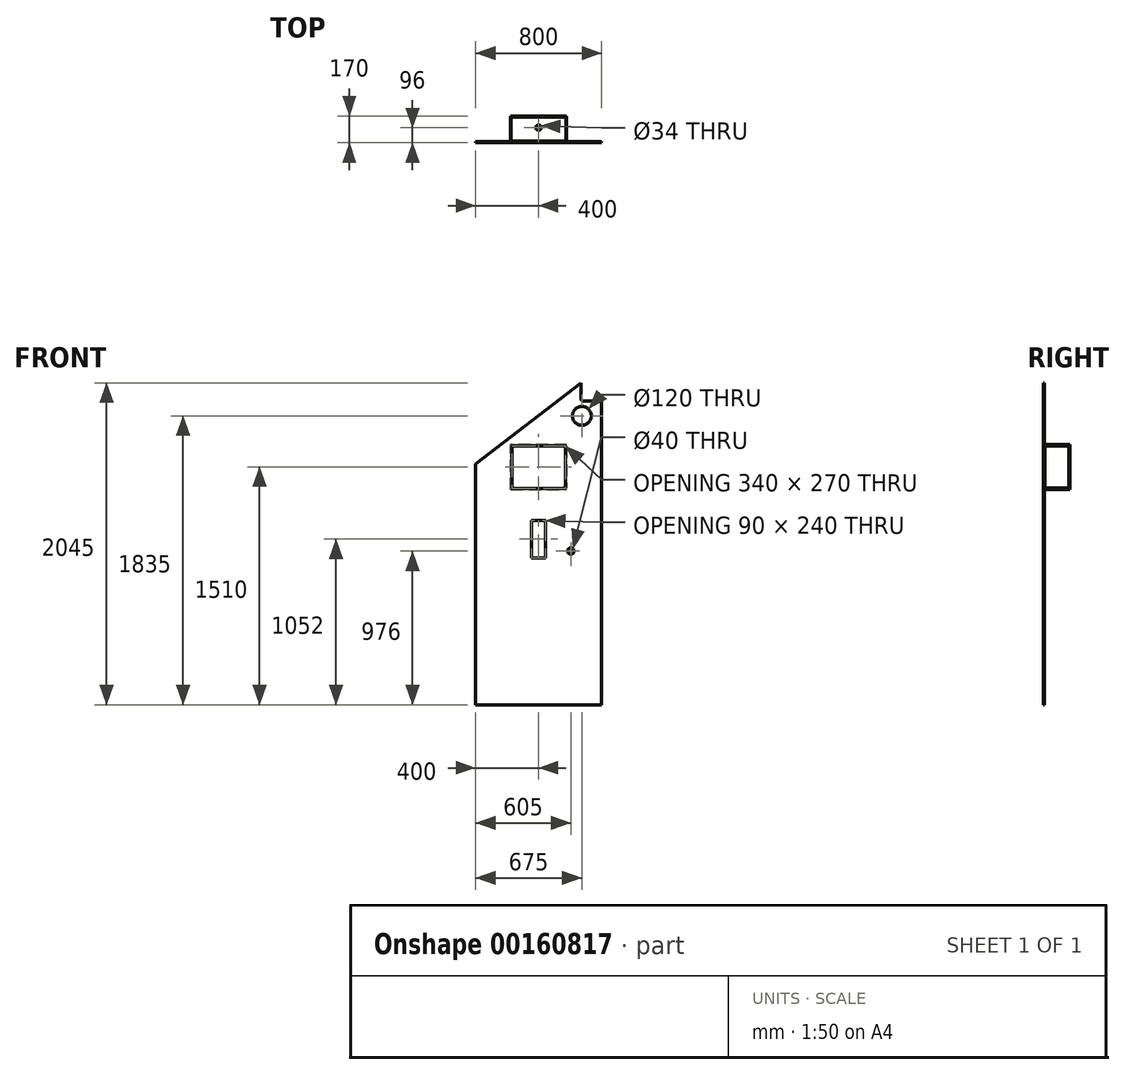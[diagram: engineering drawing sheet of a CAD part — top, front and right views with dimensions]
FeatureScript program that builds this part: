
annotation { "Feature Type Name" : "Feature", "Feature Type Description" : "" }
export const myFeature = defineFeature(function(context is Context, id is Id, definition is map)
    precondition{}
    {
        {
            var Q0;
            Q0=qCreatedBy(makeId("Front.planeOp"),FACE);
            var sketch = newSketch(context, id + "F0", { "sketchPlane" : qUnion([Q0])});
            skLineSegment(sketch, "E0.bottom", {"start": v(0, 0) * mm, "end": v(800, 0) * mm});
            skLineSegment(sketch, "E0.top", {"start": v(683, 1930) * mm, "end": v(800, 1930) * mm});
            skLineSegment(sketch, "E0.left", {"start": v(0, 0) * mm, "end": v(0, 1530) * mm});
            skLineSegment(sketch, "E0.right", {"start": v(800, 0) * mm, "end": v(800, 1930) * mm});
            skLineSegment(sketch, "E1", {"start": v(670, 2045) * mm, "end": v(0, 1530) * mm});
            skLineSegment(sketch, "E2.bottom", {"start": v(243, 1645) * mm, "end": v(557, 1645) * mm});
            skLineSegment(sketch, "E2.top", {"start": v(243, 1375) * mm, "end": v(557, 1375) * mm});
            skLineSegment(sketch, "E2.left", {"start": v(230, 1632) * mm, "end": v(230, 1388) * mm});
            skLineSegment(sketch, "E2.right", {"start": v(570, 1632) * mm, "end": v(570, 1388) * mm});
            skCircle(sketch, "E3", {"center": v(675, 1835) * mm, "radius": 60 * mm});
            skLineSegment(sketch, "E4.bottom", {"start": v(361, 1172) * mm, "end": v(439, 1172) * mm});
            skLineSegment(sketch, "E4.top", {"start": v(361, 932) * mm, "end": v(439, 932) * mm});
            skLineSegment(sketch, "E4.left", {"start": v(355, 1166) * mm, "end": v(355, 938) * mm});
            skLineSegment(sketch, "E4.right", {"start": v(445, 1166) * mm, "end": v(445, 938) * mm});
            skCircle(sketch, "E5", {"center": v(605, 976) * mm, "radius": 20 * mm});
            skLineSegment(sketch, "E6", {"start": v(400, 1172) * mm, "end": v(400, 932) * mm, "construction": true});
            skLineSegment(sketch, "E7", {"start": v(355, 1052) * mm, "end": v(445, 1052) * mm, "construction": true});
            skLineSegment(sketch, "E8", {"start": v(670, 1943) * mm, "end": v(670, 2045) * mm});
            skPoint(sketch, "E9.visualSharp", {"position": v(230, 1645) * mm});
            skArc(sketch, "E9.filletArc", {"start": v(243, 1645) * mm, "mid": v(233.8, 1641.2) * mm, "end": v(230, 1632) * mm});
            skPoint(sketch, "E10.visualSharp", {"position": v(570, 1645) * mm});
            skArc(sketch, "E10.filletArc", {"start": v(570, 1632) * mm, "mid": v(566.2, 1641.2) * mm, "end": v(557, 1645) * mm});
            skPoint(sketch, "E11.visualSharp", {"position": v(570, 1375) * mm});
            skArc(sketch, "E11.filletArc", {"start": v(557, 1375) * mm, "mid": v(566.2, 1378.8) * mm, "end": v(570, 1388) * mm});
            skPoint(sketch, "E12.visualSharp", {"position": v(230, 1375) * mm});
            skArc(sketch, "E12.filletArc", {"start": v(230, 1388) * mm, "mid": v(233.8, 1378.8) * mm, "end": v(243, 1375) * mm});
            skPoint(sketch, "E13.visualSharp", {"position": v(670, 1930) * mm});
            skArc(sketch, "E13.filletArc", {"start": v(670, 1943) * mm, "mid": v(673.8, 1933.8) * mm, "end": v(683, 1930) * mm});
            skPoint(sketch, "E14.visualSharp", {"position": v(355, 1172) * mm});
            skArc(sketch, "E14.filletArc", {"start": v(361, 1172) * mm, "mid": v(356.76, 1170.24) * mm, "end": v(355, 1166) * mm});
            skPoint(sketch, "E15.visualSharp", {"position": v(445, 1172) * mm});
            skArc(sketch, "E15.filletArc", {"start": v(445, 1166) * mm, "mid": v(443.24, 1170.24) * mm, "end": v(439, 1172) * mm});
            skPoint(sketch, "E16.visualSharp", {"position": v(445, 932) * mm});
            skArc(sketch, "E16.filletArc", {"start": v(439, 932) * mm, "mid": v(443.24, 933.76) * mm, "end": v(445, 938) * mm});
            skPoint(sketch, "E17.visualSharp", {"position": v(355, 932) * mm});
            skArc(sketch, "E17.filletArc", {"start": v(355, 938) * mm, "mid": v(356.76, 933.76) * mm, "end": v(361, 932) * mm});
            skLineSegment(sketch, "E18", {"start": v(400, 1645) * mm, "end": v(400, 1375) * mm, "construction": true});
            skLineSegment(sketch, "E19", {"start": v(230, 1510) * mm, "end": v(570, 1510) * mm, "construction": true});
            skSolve(sketch);
        }
        {
            var Q0;
            Q0=qSketchRegion(id+"F0",true);
            extrude(context, id + "F1", {"entities" : qUnion([Q0]), "depth" : 8 * mm});
        }
        {
            var Q0;
            Q0=makeQuery(id+"F1.opExtrude","SWEPT_FACE",FACE,{"disambiguationData":[OSD([sQuery(id+"F0.wireOp",EDGE,"E2.top")])]});
            var sketch = newSketch(context, id + "F2", { "sketchPlane" : qUnion([Q0])});
            skLineSegment(sketch, "E20.bottom", {"start": v(225, 3) * mm, "end": v(575, 3) * mm});
            skLineSegment(sketch, "E20.top", {"start": v(225, 154) * mm, "end": v(575, 154) * mm});
            skLineSegment(sketch, "E20.left", {"start": v(225, 3) * mm, "end": v(225, 154) * mm});
            skLineSegment(sketch, "E20.right", {"start": v(575, 3) * mm, "end": v(575, 154) * mm});
            skSolve(sketch);
        }
        {
            var Q0;
            Q0=qSketchRegion(id+"F2",true);
            extrude(context, id + "F3", {"entities" : qUnion([Q0]), "oppositeDirection" : true, "depth" : 8 * mm});
        }
        {
            var Q0;
            Q0=makeQuery(id+"F3.opExtrude","SWEPT_BODY",BODY,{"disambiguationData":[OSD([sQuery(id+"F2.wireOp",EDGE,"E20.bottom"),sQuery(id+"F2.wireOp",EDGE,"E20.top"),sQuery(id+"F2.wireOp",EDGE,"E20.left"),sQuery(id+"F2.wireOp",EDGE,"E20.right")])]});
            transform(context, id + "F4", {"entities" : qUnion([Q0]), "transformType" : TransformType.TRANSLATION_3D, "dx" : 0 * mm, "dy" : 0 * mm, "dz" : 278 * mm, "makeCopy" : true});
        }
        {
            var Q0;
            Q0=makeQuery(id+"F4.opPattern","COPY",FACE,{"derivedFrom":makeQuery(id+"F3.opExtrude","CAP_FACE",FACE,{"disambiguationData":[OSD([sQuery(id+"F2.wireOp",EDGE,"E20.bottom"),sQuery(id+"F2.wireOp",EDGE,"E20.top"),sQuery(id+"F2.wireOp",EDGE,"E20.left"),sQuery(id+"F2.wireOp",EDGE,"E20.right")])],"isStart":false}),"instanceName":"1"});
            var sketch = newSketch(context, id + "F5", { "sketchPlane" : qUnion([Q0])});
            skPoint(sketch, "E21", {"position": v(400, -88) * mm});
            skLineSegment(sketch, "E22", {"start": v(400, 0) * mm, "end": v(400, -154) * mm, "construction": true});
            skSolve(sketch);
        }
        {
            var Q0;
            Q0=sQuery(id+"F5.wireOp",VERTEX,"E21");
            var Q1;
            Q1=makeQuery(id+"F4.opPattern","COPY",BODY,{"derivedFrom":makeQuery(id+"F3.opExtrude","SWEPT_BODY",BODY,{"disambiguationData":[OSD([sQuery(id+"F2.wireOp",EDGE,"E20.bottom"),sQuery(id+"F2.wireOp",EDGE,"E20.top"),sQuery(id+"F2.wireOp",EDGE,"E20.left"),sQuery(id+"F2.wireOp",EDGE,"E20.right")])]}),"instanceName":"1"});
            hole(context, id + "F6", {"style" : HoleStyle.SIMPLE, "endStyle" : HoleEndStyle.THROUGH, "holeDiameter" : 34 * mm, "startFromSketch" : true, "locations" : qUnion([Q0]), "scope" : qUnion([Q1]), "isTappedThrough" : true});
        }
        {
            var Q0;
            Q0=makeQuery(id+"F1.opExtrude","SWEPT_FACE",FACE,{"disambiguationData":[OSD([sQuery(id+"F0.wireOp",EDGE,"E2.left")])]});
            var sketch = newSketch(context, id + "F7", { "sketchPlane" : qUnion([Q0])});
            skLineSegment(sketch, "E23.bottom", {"start": v(3, 1642) * mm, "end": v(154, 1642) * mm});
            skLineSegment(sketch, "E23.top", {"start": v(3, 1378) * mm, "end": v(154, 1378) * mm});
            skLineSegment(sketch, "E23.left", {"start": v(3, 1642) * mm, "end": v(3, 1378) * mm});
            skLineSegment(sketch, "E23.right", {"start": v(154, 1642) * mm, "end": v(154, 1378) * mm});
            skSolve(sketch);
        }
        {
            var Q0;
            Q0=qSketchRegion(id+"F7",true);
            extrude(context, id + "F8", {"entities" : qUnion([Q0]), "oppositeDirection" : true, "depth" : 8 * mm});
        }
        {
            var Q0;
            Q0=makeQuery(id+"F1.opExtrude","SWEPT_FACE",FACE,{"disambiguationData":[OSD([sQuery(id+"F0.wireOp",EDGE,"E2.left")])]});
            var Q1;
            Q1=makeQuery(id+"F1.opExtrude","SWEPT_FACE",FACE,{"disambiguationData":[OSD([sQuery(id+"F0.wireOp",EDGE,"E2.right")])]});
            cPlane(context, id + "F9", {"entities" : qUnion([Q0, Q1]), "cplaneType" : CPlaneType.MID_PLANE, "offset" : 25 * mm, "width" : 150 * mm, "height" : 150 * mm});
        }
        {
            var Q0;
            Q0=makeQuery(id+"F8.opExtrude","SWEPT_BODY",BODY,{"disambiguationData":[OSD([sQuery(id+"F7.wireOp",EDGE,"E23.bottom"),sQuery(id+"F7.wireOp",EDGE,"E23.top"),sQuery(id+"F7.wireOp",EDGE,"E23.left"),sQuery(id+"F7.wireOp",EDGE,"E23.right")])]});
            var Q1;
            Q1=qCreatedBy(id+"F9.planeOp",FACE);
            mirror(context, id + "F10", {"entities" : qUnion([Q0]), "mirrorPlane" : qUnion([Q1])});
        }
        {
            var Q0;
            Q0=makeQuery(id+"F3.opExtrude","SWEPT_FACE",FACE,{"disambiguationData":[OSD([sQuery(id+"F2.wireOp",EDGE,"E20.top")])]});
            var sketch = newSketch(context, id + "F11", { "sketchPlane" : qUnion([Q0])});
            skLineSegment(sketch, "E24.bottom", {"start": v(-578, 1653) * mm, "end": v(-222, 1653) * mm});
            skLineSegment(sketch, "E24.top", {"start": v(-578, 1367) * mm, "end": v(-222, 1367) * mm});
            skLineSegment(sketch, "E24.left", {"start": v(-222, 1367) * mm, "end": v(-222, 1653) * mm});
            skLineSegment(sketch, "E24.right", {"start": v(-578, 1367) * mm, "end": v(-578, 1653) * mm});
            skLineSegment(sketch, "E25", {"start": v(-400, 1375) * mm, "end": v(-400, 1645) * mm, "construction": true});
            skPoint(sketch, "E25.endSnap0", {"position": v(-400, 1375) * mm});
            skLineSegment(sketch, "E26", {"start": v(-570, 1510) * mm, "end": v(-230, 1510) * mm, "construction": true});
            skPoint(sketch, "E26.endSnap0", {"position": v(-222, 1510) * mm});
            skPoint(sketch, "E27.orphan", {"position": v(-400, 1510) * mm});
            skSolve(sketch);
        }
        {
            var Q0;
            Q0=makeQuery(id+"F11.imprint","IMPRINT",FACE,{"disambiguationData":[TD([[makeQuery(id+"F11.imprint","IMPRINT",EDGE,{"derivedFrom":sQuery(id+"F11.wireOp",EDGE,"E24.bottom")}),-1.0]])]});
            var Q1;
            {var subQ1=sQuery(id+"F2.wireOp",EDGE,"E20.top");Q1=makeQuery(id+"F11.imprint","IMPRINT",FACE,{"disambiguationData":[TD([[makeQuery(id+"F11.imprint","IMPRINT",EDGE,{"derivedFrom":makeQuery(id+"F3.opExtrude","CAP_EDGE",EDGE,{"disambiguationData":[OSD([subQ1])],"isStart":true})}),1.0]])]});}
            extrude(context, id + "F12", {"entities" : qUnion([Q0, Q1]), "depth" : 8 * mm});
        }
    });
